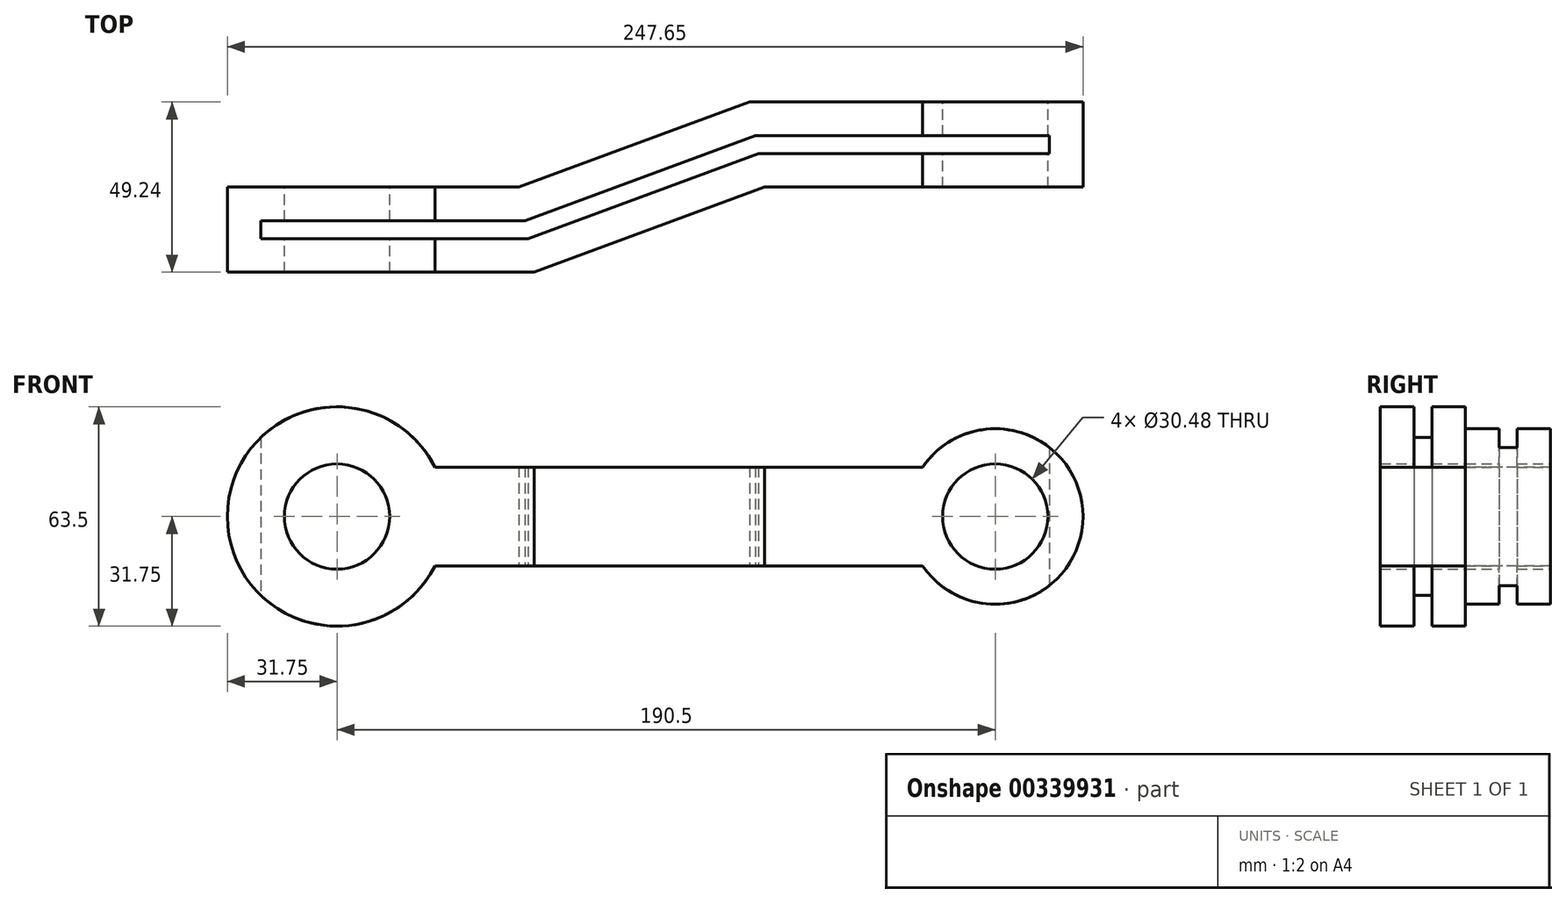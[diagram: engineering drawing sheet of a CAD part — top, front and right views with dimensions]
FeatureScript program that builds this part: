
annotation { "Feature Type Name" : "Feature", "Feature Type Description" : "" }
export const myFeature = defineFeature(function(context is Context, id is Id, definition is map)
    precondition{}
    {
        {
            var Q0;
            Q0=qCreatedBy(makeId("Front.planeOp"),FACE);
            var sketch = newSketch(context, id + "F0", { "sketchPlane" : qUnion([Q0])});
            skCircle(sketch, "E0", {"center": v(0, 0) * mm, "radius": 25.4 * mm});
            skCircle(sketch, "E1", {"center": v(0, 0) * mm, "radius": 15.24 * mm});
            skCircle(sketch, "E2", {"center": v(-190.5, 0) * mm, "radius": 15.24 * mm});
            skCircle(sketch, "E3", {"center": v(-190.5, 0) * mm, "radius": 31.75 * mm});
            skLineSegment(sketch, "E4", {"start": v(0, 0) * mm, "end": v(-190.5, 0) * mm, "construction": true});
            skLineSegment(sketch, "E5", {"start": v(-162.15, 14.29) * mm, "end": v(-21, 14.29) * mm});
            skLineSegment(sketch, "E6.MirrorCS", {"start": v(-162.15, -14.29) * mm, "end": v(-21, -14.29) * mm});
            skSolve(sketch);
        }
        {
            var Q0;
            Q0 = qSketchRegion(id + "F0", true);
            extrude(context, id + "F1", {"entities" : qUnion([Q0]), "depth" : 63.5 * mm});
        }
        {
            var Q0;
            Q0=qCreatedBy(makeId("Top.planeOp"),FACE);
            var sketch = newSketch(context, id + "F2", { "sketchPlane" : qUnion([Q0])});
            skLineSegment(sketch, "E7", {"start": v(-222.25, -24.62) * mm, "end": v(-137.88, -24.62) * mm});
            skLineSegment(sketch, "E8", {"start": v(-137.88, -24.62) * mm, "end": v(-71.13, 0) * mm});
            skLineSegment(sketch, "E9", {"start": v(-71.13, 0) * mm, "end": v(25.4, 0) * mm});
            skLineSegment(sketch, "E10.0", {"start": v(-66.73, -24.62) * mm, "end": v(25.4, -24.62) * mm});
            skLineSegment(sketch, "E10.1", {"start": v(-133.49, -49.24) * mm, "end": v(-66.73, -24.62) * mm});
            skLineSegment(sketch, "E10.2", {"start": v(-222.25, -49.24) * mm, "end": v(-133.49, -49.24) * mm});
            skLineSegment(sketch, "E11", {"start": v(-222.25, -24.62) * mm, "end": v(-222.25, -49.24) * mm});
            skLineSegment(sketch, "E12", {"start": v(25.4, 0) * mm, "end": v(25.4, -24.62) * mm});
            skLineSegment(sketch, "E13", {"start": v(-222.25, -63.5) * mm, "end": v(-222.25, 0) * mm});
            skLineSegment(sketch, "E14", {"start": v(25.4, 0) * mm, "end": v(25.4, -63.5) * mm});
            skLineSegment(sketch, "E15.0", {"start": v(-212.52, -39.51) * mm, "end": v(-135.23, -39.51) * mm});
            skLineSegment(sketch, "E15.1", {"start": v(-212.52, -34.35) * mm, "end": v(-212.52, -39.51) * mm});
            skLineSegment(sketch, "E15.2", {"start": v(-135.23, -39.51) * mm, "end": v(-68.47, -14.89) * mm});
            skLineSegment(sketch, "E15.3", {"start": v(-212.52, -34.35) * mm, "end": v(-136.15, -34.35) * mm});
            skLineSegment(sketch, "E15.4", {"start": v(-68.47, -14.89) * mm, "end": v(15.67, -14.89) * mm});
            skLineSegment(sketch, "E15.5", {"start": v(15.67, -9.73) * mm, "end": v(15.67, -14.89) * mm});
            skLineSegment(sketch, "E15.6", {"start": v(-69.4, -9.73) * mm, "end": v(15.67, -9.73) * mm});
            skLineSegment(sketch, "E15.7", {"start": v(-136.15, -34.35) * mm, "end": v(-69.4, -9.73) * mm});
            skSolve(sketch);
        }
        {
            var Q0;
            Q0 = qSketchRegion(id + "F2", true);
            extrude(context, id + "F3", {"entities" : qUnion([Q0]), "operationType" : NewBodyOperationType.INTERSECT, "endBound" : BoundingType.SYMMETRIC, "depth" : 63.5 * mm});
        }
    });
